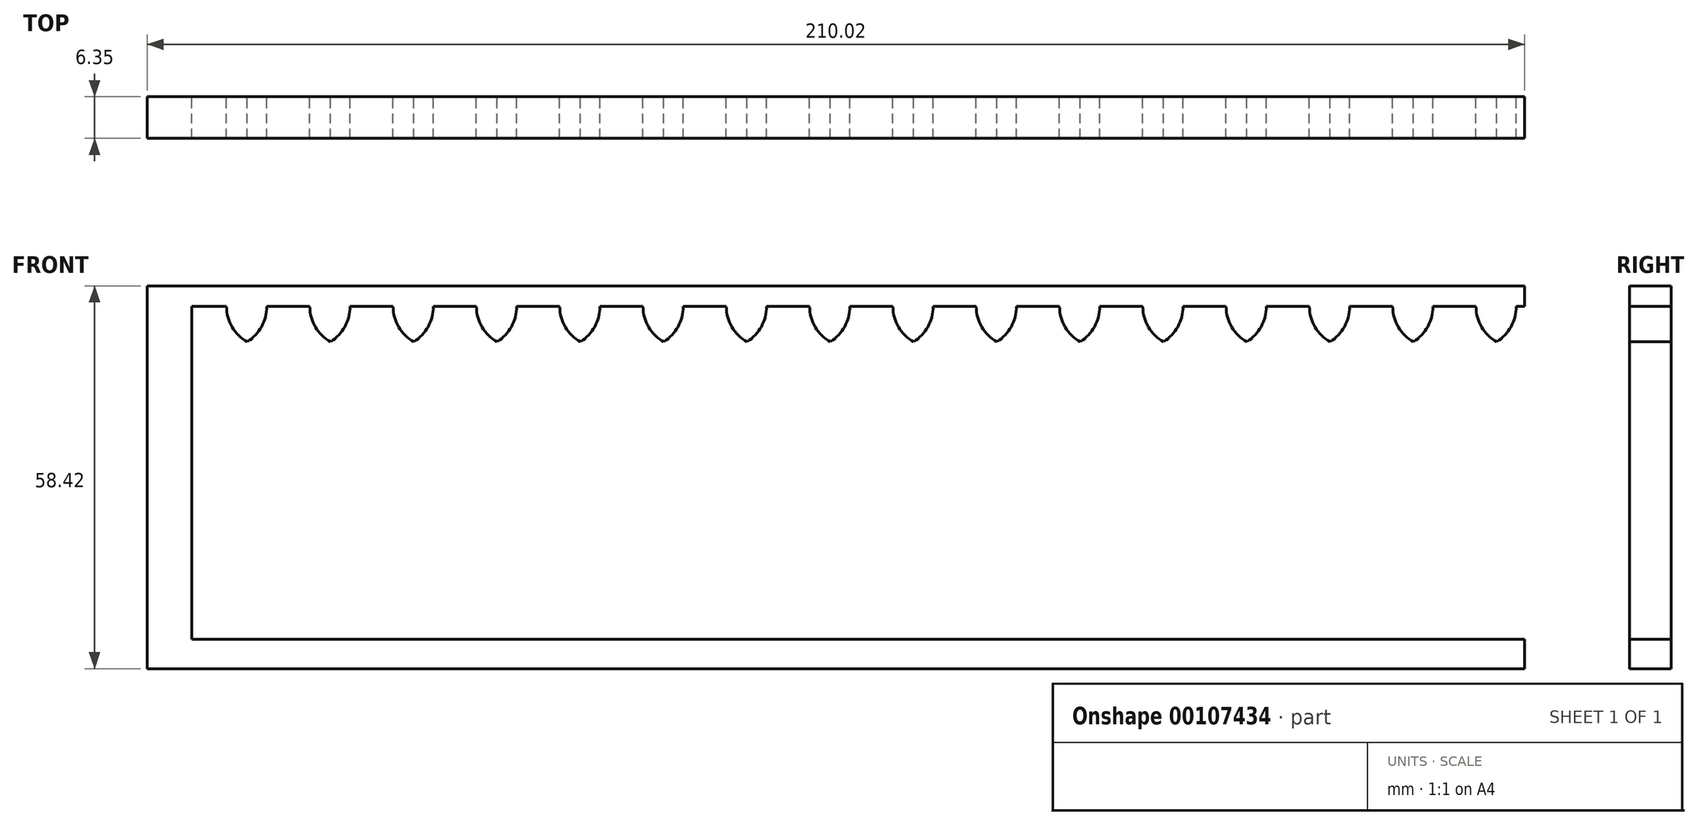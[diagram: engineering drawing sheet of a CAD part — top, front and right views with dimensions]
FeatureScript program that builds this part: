
annotation { "Feature Type Name" : "Feature", "Feature Type Description" : "" }
export const myFeature = defineFeature(function(context is Context, id is Id, definition is map)
    precondition{}
    {
        {
            var Q0;
            Q0=qCreatedBy(makeId("Front.planeOp"),FACE);
            var sketch = newSketch(context, id + "F0", { "sketchPlane" : qUnion([Q0])});
            skLineSegment(sketch, "E0.bottom", {"start": v(-100.17, 36.3) * mm, "end": v(103.03, 36.3) * mm});
            skLineSegment(sketch, "E0.top", {"start": v(-100.17, -14.5) * mm, "end": v(103.03, -14.5) * mm});
            skLineSegment(sketch, "E0.left", {"start": v(-100.17, 36.3) * mm, "end": v(-100.17, -14.5) * mm});
            skArc(sketch, "E1", {"start": v(-91.7, 30.93) * mm, "mid": v(-89.52, 33.23) * mm, "end": v(-88.73, 36.3) * mm});
            skArc(sketch, "E2", {"start": v(-94.87, 36.3) * mm, "mid": v(-94.02, 33.18) * mm, "end": v(-91.7, 30.93) * mm});
            skArc(sketch, "E3.1.0.0", {"start": v(-79, 30.93) * mm, "mid": v(-76.82, 33.23) * mm, "end": v(-76.03, 36.3) * mm});
            skArc(sketch, "E3.1.0.1", {"start": v(-82.17, 36.3) * mm, "mid": v(-81.32, 33.18) * mm, "end": v(-79, 30.93) * mm});
            skArc(sketch, "E3.2.0.0", {"start": v(-66.3, 30.93) * mm, "mid": v(-64.12, 33.23) * mm, "end": v(-63.33, 36.3) * mm});
            skArc(sketch, "E3.2.0.1", {"start": v(-69.47, 36.3) * mm, "mid": v(-68.62, 33.18) * mm, "end": v(-66.3, 30.93) * mm});
            skArc(sketch, "E3.3.0.0", {"start": v(-53.6, 30.93) * mm, "mid": v(-51.42, 33.23) * mm, "end": v(-50.63, 36.3) * mm});
            skArc(sketch, "E3.3.0.1", {"start": v(-56.77, 36.3) * mm, "mid": v(-55.92, 33.18) * mm, "end": v(-53.6, 30.93) * mm});
            skArc(sketch, "E3.4.0.0", {"start": v(-40.9, 30.93) * mm, "mid": v(-38.72, 33.23) * mm, "end": v(-37.93, 36.3) * mm});
            skArc(sketch, "E3.4.0.1", {"start": v(-44.07, 36.3) * mm, "mid": v(-43.22, 33.18) * mm, "end": v(-40.9, 30.93) * mm});
            skArc(sketch, "E3.5.0.0", {"start": v(-28.2, 30.93) * mm, "mid": v(-26.02, 33.23) * mm, "end": v(-25.23, 36.3) * mm});
            skArc(sketch, "E3.5.0.1", {"start": v(-31.37, 36.3) * mm, "mid": v(-30.52, 33.18) * mm, "end": v(-28.2, 30.93) * mm});
            skArc(sketch, "E3.6.0.0", {"start": v(-15.5, 30.93) * mm, "mid": v(-13.32, 33.23) * mm, "end": v(-12.53, 36.3) * mm});
            skArc(sketch, "E3.6.0.1", {"start": v(-18.67, 36.3) * mm, "mid": v(-17.82, 33.18) * mm, "end": v(-15.5, 30.93) * mm});
            skArc(sketch, "E3.7.0.0", {"start": v(-2.8, 30.93) * mm, "mid": v(-0.62, 33.23) * mm, "end": v(0.17, 36.3) * mm});
            skArc(sketch, "E3.7.0.1", {"start": v(-5.97, 36.3) * mm, "mid": v(-5.12, 33.18) * mm, "end": v(-2.8, 30.93) * mm});
            skArc(sketch, "E3.8.0.0", {"start": v(9.9, 30.93) * mm, "mid": v(12.08, 33.23) * mm, "end": v(12.87, 36.3) * mm});
            skArc(sketch, "E3.8.0.1", {"start": v(6.73, 36.3) * mm, "mid": v(7.58, 33.18) * mm, "end": v(9.9, 30.93) * mm});
            skArc(sketch, "E3.9.0.0", {"start": v(22.6, 30.93) * mm, "mid": v(24.78, 33.23) * mm, "end": v(25.57, 36.3) * mm});
            skArc(sketch, "E3.9.0.1", {"start": v(19.43, 36.3) * mm, "mid": v(20.28, 33.18) * mm, "end": v(22.6, 30.93) * mm});
            skArc(sketch, "E3.10.0.0", {"start": v(35.3, 30.93) * mm, "mid": v(37.48, 33.23) * mm, "end": v(38.27, 36.3) * mm});
            skArc(sketch, "E3.10.0.1", {"start": v(32.13, 36.3) * mm, "mid": v(32.98, 33.18) * mm, "end": v(35.3, 30.93) * mm});
            skArc(sketch, "E3.11.0.0", {"start": v(48, 30.93) * mm, "mid": v(50.18, 33.23) * mm, "end": v(50.97, 36.3) * mm});
            skArc(sketch, "E3.11.0.1", {"start": v(44.83, 36.3) * mm, "mid": v(45.68, 33.18) * mm, "end": v(48, 30.93) * mm});
            skArc(sketch, "E3.12.0.0", {"start": v(60.7, 30.93) * mm, "mid": v(62.88, 33.23) * mm, "end": v(63.67, 36.3) * mm});
            skArc(sketch, "E3.12.0.1", {"start": v(57.53, 36.3) * mm, "mid": v(58.38, 33.18) * mm, "end": v(60.7, 30.93) * mm});
            skArc(sketch, "E3.13.0.0", {"start": v(73.4, 30.93) * mm, "mid": v(75.58, 33.23) * mm, "end": v(76.37, 36.3) * mm});
            skArc(sketch, "E3.13.0.1", {"start": v(70.23, 36.3) * mm, "mid": v(71.08, 33.18) * mm, "end": v(73.4, 30.93) * mm});
            skArc(sketch, "E3.14.0.0", {"start": v(86.1, 30.93) * mm, "mid": v(88.28, 33.23) * mm, "end": v(89.07, 36.3) * mm});
            skArc(sketch, "E3.14.0.1", {"start": v(82.93, 36.3) * mm, "mid": v(83.78, 33.18) * mm, "end": v(86.1, 30.93) * mm});
            skArc(sketch, "E3.15.0.0", {"start": v(98.8, 30.93) * mm, "mid": v(100.98, 33.23) * mm, "end": v(101.77, 36.3) * mm});
            skArc(sketch, "E3.15.0.1", {"start": v(95.63, 36.3) * mm, "mid": v(96.48, 33.18) * mm, "end": v(98.8, 30.93) * mm});
            skLineSegment(sketch, "E3.direction1", {"start": v(-91.7, 30.93) * mm, "end": v(-79, 30.93) * mm, "construction": true});
            skArc(sketch, "E4.MirrorCS", {"start": v(-94.87, -14.5) * mm, "mid": v(-94.02, -11.38) * mm, "end": v(-91.7, -9.13) * mm});
            skArc(sketch, "E5.MirrorCS", {"start": v(-91.7, -9.13) * mm, "mid": v(-89.52, -11.43) * mm, "end": v(-88.73, -14.5) * mm});
            skArc(sketch, "E6.MirrorCS", {"start": v(-82.17, -14.5) * mm, "mid": v(-81.32, -11.38) * mm, "end": v(-79, -9.13) * mm});
            skArc(sketch, "E7.MirrorCS", {"start": v(-79, -9.13) * mm, "mid": v(-76.82, -11.43) * mm, "end": v(-76.03, -14.5) * mm});
            skArc(sketch, "E8.MirrorCS", {"start": v(-69.47, -14.5) * mm, "mid": v(-68.62, -11.38) * mm, "end": v(-66.3, -9.13) * mm});
            skArc(sketch, "E9.MirrorCS", {"start": v(-66.3, -9.13) * mm, "mid": v(-64.12, -11.43) * mm, "end": v(-63.33, -14.5) * mm});
            skArc(sketch, "E10.MirrorCS", {"start": v(-56.77, -14.5) * mm, "mid": v(-55.92, -11.38) * mm, "end": v(-53.6, -9.13) * mm});
            skArc(sketch, "E11.MirrorCS", {"start": v(-53.6, -9.13) * mm, "mid": v(-51.42, -11.43) * mm, "end": v(-50.63, -14.5) * mm});
            skArc(sketch, "E12.MirrorCS", {"start": v(-44.07, -14.5) * mm, "mid": v(-43.22, -11.38) * mm, "end": v(-40.9, -9.13) * mm});
            skArc(sketch, "E13.MirrorCS", {"start": v(-40.9, -9.13) * mm, "mid": v(-38.72, -11.43) * mm, "end": v(-37.93, -14.5) * mm});
            skArc(sketch, "E14.MirrorCS", {"start": v(-31.37, -14.5) * mm, "mid": v(-30.52, -11.38) * mm, "end": v(-28.2, -9.13) * mm});
            skArc(sketch, "E15.MirrorCS", {"start": v(-28.2, -9.13) * mm, "mid": v(-26.02, -11.43) * mm, "end": v(-25.23, -14.5) * mm});
            skArc(sketch, "E16.MirrorCS", {"start": v(-18.67, -14.5) * mm, "mid": v(-17.82, -11.38) * mm, "end": v(-15.5, -9.13) * mm});
            skArc(sketch, "E17.MirrorCS", {"start": v(-15.5, -9.13) * mm, "mid": v(-13.32, -11.43) * mm, "end": v(-12.53, -14.5) * mm});
            skArc(sketch, "E18.MirrorCS", {"start": v(-5.97, -14.5) * mm, "mid": v(-5.12, -11.38) * mm, "end": v(-2.8, -9.13) * mm});
            skArc(sketch, "E19.MirrorCS", {"start": v(-2.8, -9.13) * mm, "mid": v(-0.62, -11.43) * mm, "end": v(0.17, -14.5) * mm});
            skArc(sketch, "E20.MirrorCS", {"start": v(6.73, -14.5) * mm, "mid": v(7.58, -11.38) * mm, "end": v(9.9, -9.13) * mm});
            skArc(sketch, "E21.MirrorCS", {"start": v(9.9, -9.13) * mm, "mid": v(12.08, -11.43) * mm, "end": v(12.87, -14.5) * mm});
            skArc(sketch, "E22.MirrorCS", {"start": v(19.43, -14.5) * mm, "mid": v(20.28, -11.38) * mm, "end": v(22.6, -9.13) * mm});
            skArc(sketch, "E23.MirrorCS", {"start": v(22.6, -9.13) * mm, "mid": v(24.78, -11.43) * mm, "end": v(25.57, -14.5) * mm});
            skArc(sketch, "E24.MirrorCS", {"start": v(32.13, -14.5) * mm, "mid": v(32.98, -11.38) * mm, "end": v(35.3, -9.13) * mm});
            skArc(sketch, "E25.MirrorCS", {"start": v(35.3, -9.13) * mm, "mid": v(37.48, -11.43) * mm, "end": v(38.27, -14.5) * mm});
            skArc(sketch, "E26.MirrorCS", {"start": v(44.83, -14.5) * mm, "mid": v(45.68, -11.38) * mm, "end": v(48, -9.13) * mm});
            skArc(sketch, "E27.MirrorCS", {"start": v(48, -9.13) * mm, "mid": v(50.18, -11.43) * mm, "end": v(50.97, -14.5) * mm});
            skArc(sketch, "E28.MirrorCS", {"start": v(57.53, -14.5) * mm, "mid": v(58.38, -11.38) * mm, "end": v(60.7, -9.13) * mm});
            skArc(sketch, "E29.MirrorCS", {"start": v(60.7, -9.13) * mm, "mid": v(62.88, -11.43) * mm, "end": v(63.67, -14.5) * mm});
            skArc(sketch, "E30.MirrorCS", {"start": v(70.23, -14.5) * mm, "mid": v(71.08, -11.38) * mm, "end": v(73.4, -9.13) * mm});
            skArc(sketch, "E31.MirrorCS", {"start": v(73.4, -9.13) * mm, "mid": v(75.58, -11.43) * mm, "end": v(76.37, -14.5) * mm});
            skArc(sketch, "E32.MirrorCS", {"start": v(82.93, -14.5) * mm, "mid": v(83.78, -11.38) * mm, "end": v(86.1, -9.13) * mm});
            skArc(sketch, "E33.MirrorCS", {"start": v(86.1, -9.13) * mm, "mid": v(88.28, -11.43) * mm, "end": v(89.07, -14.5) * mm});
            skArc(sketch, "E34.MirrorCS", {"start": v(95.63, -14.5) * mm, "mid": v(96.48, -11.38) * mm, "end": v(98.8, -9.13) * mm});
            skArc(sketch, "E35.MirrorCS", {"start": v(98.8, -9.13) * mm, "mid": v(100.98, -11.43) * mm, "end": v(101.77, -14.5) * mm});
            skLineSegment(sketch, "E36.bottom", {"start": v(-107, 39.46) * mm, "end": v(103.03, 39.46) * mm});
            skLineSegment(sketch, "E36.top", {"start": v(-107, -18.96) * mm, "end": v(103.03, -18.96) * mm});
            skLineSegment(sketch, "E36.left", {"start": v(-107, 39.46) * mm, "end": v(-107, -18.96) * mm});
            skLineSegment(sketch, "E37", {"start": v(103.03, 36.3) * mm, "end": v(103.03, 39.46) * mm});
            skLineSegment(sketch, "E38", {"start": v(103.03, -14.5) * mm, "end": v(103.03, -18.96) * mm});
            skSolve(sketch);
        }
        {
            var Q0;
            {var subQ30=sQuery(id+"F0.wireOp",EDGE,"E0.left");Q0=makeQuery(id+"F0.imprint","IMPRINT",FACE,{"disambiguationData":[TD([[makeQuery(id+"F0.imprint","IMPRINT",EDGE,{"derivedFrom":subQ30}),-1.0]])]});}
            var Q1;
            {var subQ0=sQuery(id+"F0.wireOp",EDGE,"E1");Q1=makeQuery(id+"F0.imprint","IMPRINT",FACE,{"disambiguationData":[TD([[makeQuery(id+"F0.imprint","IMPRINT",EDGE,{"derivedFrom":subQ0}),1.0]])]});}
            var Q2;
            {var subQ0=sQuery(id+"F0.wireOp",EDGE,"E3.1.0.0");Q2=makeQuery(id+"F0.imprint","IMPRINT",FACE,{"disambiguationData":[TD([[makeQuery(id+"F0.imprint","IMPRINT",EDGE,{"derivedFrom":subQ0}),1.0]])]});}
            var Q3;
            {var subQ0=sQuery(id+"F0.wireOp",EDGE,"E3.2.0.0");Q3=makeQuery(id+"F0.imprint","IMPRINT",FACE,{"disambiguationData":[TD([[makeQuery(id+"F0.imprint","IMPRINT",EDGE,{"derivedFrom":subQ0}),1.0]])]});}
            var Q4;
            {var subQ0=sQuery(id+"F0.wireOp",EDGE,"E3.3.0.0");Q4=makeQuery(id+"F0.imprint","IMPRINT",FACE,{"disambiguationData":[TD([[makeQuery(id+"F0.imprint","IMPRINT",EDGE,{"derivedFrom":subQ0}),1.0]])]});}
            var Q5;
            {var subQ0=sQuery(id+"F0.wireOp",EDGE,"E3.4.0.0");Q5=makeQuery(id+"F0.imprint","IMPRINT",FACE,{"disambiguationData":[TD([[makeQuery(id+"F0.imprint","IMPRINT",EDGE,{"derivedFrom":subQ0}),1.0]])]});}
            var Q6;
            {var subQ0=sQuery(id+"F0.wireOp",EDGE,"E3.5.0.0");Q6=makeQuery(id+"F0.imprint","IMPRINT",FACE,{"disambiguationData":[TD([[makeQuery(id+"F0.imprint","IMPRINT",EDGE,{"derivedFrom":subQ0}),1.0]])]});}
            var Q7;
            {var subQ0=sQuery(id+"F0.wireOp",EDGE,"E3.6.0.0");Q7=makeQuery(id+"F0.imprint","IMPRINT",FACE,{"disambiguationData":[TD([[makeQuery(id+"F0.imprint","IMPRINT",EDGE,{"derivedFrom":subQ0}),1.0]])]});}
            var Q8;
            {var subQ0=sQuery(id+"F0.wireOp",EDGE,"E3.7.0.0");Q8=makeQuery(id+"F0.imprint","IMPRINT",FACE,{"disambiguationData":[TD([[makeQuery(id+"F0.imprint","IMPRINT",EDGE,{"derivedFrom":subQ0}),1.0]])]});}
            var Q9;
            {var subQ0=sQuery(id+"F0.wireOp",EDGE,"E3.8.0.0");Q9=makeQuery(id+"F0.imprint","IMPRINT",FACE,{"disambiguationData":[TD([[makeQuery(id+"F0.imprint","IMPRINT",EDGE,{"derivedFrom":subQ0}),1.0]])]});}
            var Q10;
            {var subQ0=sQuery(id+"F0.wireOp",EDGE,"E3.9.0.0");Q10=makeQuery(id+"F0.imprint","IMPRINT",FACE,{"disambiguationData":[TD([[makeQuery(id+"F0.imprint","IMPRINT",EDGE,{"derivedFrom":subQ0}),1.0]])]});}
            var Q11;
            {var subQ0=sQuery(id+"F0.wireOp",EDGE,"E3.10.0.0");Q11=makeQuery(id+"F0.imprint","IMPRINT",FACE,{"disambiguationData":[TD([[makeQuery(id+"F0.imprint","IMPRINT",EDGE,{"derivedFrom":subQ0}),1.0]])]});}
            var Q12;
            {var subQ0=sQuery(id+"F0.wireOp",EDGE,"E3.11.0.0");Q12=makeQuery(id+"F0.imprint","IMPRINT",FACE,{"disambiguationData":[TD([[makeQuery(id+"F0.imprint","IMPRINT",EDGE,{"derivedFrom":subQ0}),1.0]])]});}
            var Q13;
            {var subQ0=sQuery(id+"F0.wireOp",EDGE,"E3.12.0.0");Q13=makeQuery(id+"F0.imprint","IMPRINT",FACE,{"disambiguationData":[TD([[makeQuery(id+"F0.imprint","IMPRINT",EDGE,{"derivedFrom":subQ0}),1.0]])]});}
            var Q14;
            {var subQ0=sQuery(id+"F0.wireOp",EDGE,"E3.13.0.0");Q14=makeQuery(id+"F0.imprint","IMPRINT",FACE,{"disambiguationData":[TD([[makeQuery(id+"F0.imprint","IMPRINT",EDGE,{"derivedFrom":subQ0}),1.0]])]});}
            var Q15;
            {var subQ0=sQuery(id+"F0.wireOp",EDGE,"E3.14.0.0");Q15=makeQuery(id+"F0.imprint","IMPRINT",FACE,{"disambiguationData":[TD([[makeQuery(id+"F0.imprint","IMPRINT",EDGE,{"derivedFrom":subQ0}),1.0]])]});}
            var Q16;
            {var subQ0=sQuery(id+"F0.wireOp",EDGE,"E3.15.0.0");Q16=makeQuery(id+"F0.imprint","IMPRINT",FACE,{"disambiguationData":[TD([[makeQuery(id+"F0.imprint","IMPRINT",EDGE,{"derivedFrom":subQ0}),1.0]])]});}
            var Q17;
            {var subQ0=sQuery(id+"F0.wireOp",EDGE,"E34.MirrorCS");Q17=makeQuery(id+"F0.imprint","IMPRINT",FACE,{"disambiguationData":[TD([[makeQuery(id+"F0.imprint","IMPRINT",EDGE,{"derivedFrom":subQ0}),-1.0]])]});}
            var Q18;
            {var subQ0=sQuery(id+"F0.wireOp",EDGE,"E32.MirrorCS");Q18=makeQuery(id+"F0.imprint","IMPRINT",FACE,{"disambiguationData":[TD([[makeQuery(id+"F0.imprint","IMPRINT",EDGE,{"derivedFrom":subQ0}),-1.0]])]});}
            var Q19;
            {var subQ0=sQuery(id+"F0.wireOp",EDGE,"E30.MirrorCS");Q19=makeQuery(id+"F0.imprint","IMPRINT",FACE,{"disambiguationData":[TD([[makeQuery(id+"F0.imprint","IMPRINT",EDGE,{"derivedFrom":subQ0}),-1.0]])]});}
            var Q20;
            {var subQ0=sQuery(id+"F0.wireOp",EDGE,"E28.MirrorCS");Q20=makeQuery(id+"F0.imprint","IMPRINT",FACE,{"disambiguationData":[TD([[makeQuery(id+"F0.imprint","IMPRINT",EDGE,{"derivedFrom":subQ0}),-1.0]])]});}
            var Q21;
            {var subQ0=sQuery(id+"F0.wireOp",EDGE,"E26.MirrorCS");Q21=makeQuery(id+"F0.imprint","IMPRINT",FACE,{"disambiguationData":[TD([[makeQuery(id+"F0.imprint","IMPRINT",EDGE,{"derivedFrom":subQ0}),-1.0]])]});}
            var Q22;
            {var subQ0=sQuery(id+"F0.wireOp",EDGE,"E24.MirrorCS");Q22=makeQuery(id+"F0.imprint","IMPRINT",FACE,{"disambiguationData":[TD([[makeQuery(id+"F0.imprint","IMPRINT",EDGE,{"derivedFrom":subQ0}),-1.0]])]});}
            var Q23;
            {var subQ0=sQuery(id+"F0.wireOp",EDGE,"E22.MirrorCS");Q23=makeQuery(id+"F0.imprint","IMPRINT",FACE,{"disambiguationData":[TD([[makeQuery(id+"F0.imprint","IMPRINT",EDGE,{"derivedFrom":subQ0}),-1.0]])]});}
            var Q24;
            {var subQ0=sQuery(id+"F0.wireOp",EDGE,"E20.MirrorCS");Q24=makeQuery(id+"F0.imprint","IMPRINT",FACE,{"disambiguationData":[TD([[makeQuery(id+"F0.imprint","IMPRINT",EDGE,{"derivedFrom":subQ0}),-1.0]])]});}
            var Q25;
            {var subQ0=sQuery(id+"F0.wireOp",EDGE,"E18.MirrorCS");Q25=makeQuery(id+"F0.imprint","IMPRINT",FACE,{"disambiguationData":[TD([[makeQuery(id+"F0.imprint","IMPRINT",EDGE,{"derivedFrom":subQ0}),-1.0]])]});}
            var Q26;
            {var subQ0=sQuery(id+"F0.wireOp",EDGE,"E16.MirrorCS");Q26=makeQuery(id+"F0.imprint","IMPRINT",FACE,{"disambiguationData":[TD([[makeQuery(id+"F0.imprint","IMPRINT",EDGE,{"derivedFrom":subQ0}),-1.0]])]});}
            var Q27;
            {var subQ0=sQuery(id+"F0.wireOp",EDGE,"E14.MirrorCS");Q27=makeQuery(id+"F0.imprint","IMPRINT",FACE,{"disambiguationData":[TD([[makeQuery(id+"F0.imprint","IMPRINT",EDGE,{"derivedFrom":subQ0}),-1.0]])]});}
            var Q28;
            {var subQ0=sQuery(id+"F0.wireOp",EDGE,"E12.MirrorCS");Q28=makeQuery(id+"F0.imprint","IMPRINT",FACE,{"disambiguationData":[TD([[makeQuery(id+"F0.imprint","IMPRINT",EDGE,{"derivedFrom":subQ0}),-1.0]])]});}
            var Q29;
            {var subQ0=sQuery(id+"F0.wireOp",EDGE,"E10.MirrorCS");Q29=makeQuery(id+"F0.imprint","IMPRINT",FACE,{"disambiguationData":[TD([[makeQuery(id+"F0.imprint","IMPRINT",EDGE,{"derivedFrom":subQ0}),-1.0]])]});}
            var Q30;
            {var subQ0=sQuery(id+"F0.wireOp",EDGE,"E8.MirrorCS");Q30=makeQuery(id+"F0.imprint","IMPRINT",FACE,{"disambiguationData":[TD([[makeQuery(id+"F0.imprint","IMPRINT",EDGE,{"derivedFrom":subQ0}),-1.0]])]});}
            var Q31;
            {var subQ0=sQuery(id+"F0.wireOp",EDGE,"E6.MirrorCS");Q31=makeQuery(id+"F0.imprint","IMPRINT",FACE,{"disambiguationData":[TD([[makeQuery(id+"F0.imprint","IMPRINT",EDGE,{"derivedFrom":subQ0}),-1.0]])]});}
            var Q32;
            {var subQ0=sQuery(id+"F0.wireOp",EDGE,"E4.MirrorCS");Q32=makeQuery(id+"F0.imprint","IMPRINT",FACE,{"disambiguationData":[TD([[makeQuery(id+"F0.imprint","IMPRINT",EDGE,{"derivedFrom":subQ0}),-1.0]])]});}
            extrude(context, id + "F1", {"entities" : qUnion([Q0, Q1, Q2, Q3, Q4, Q5, Q6, Q7, Q8, Q9, Q10, Q11, Q12, Q13, Q14, Q15, Q16, Q17, Q18, Q19, Q20, Q21, Q22, Q23, Q24, Q25, Q26, Q27, Q28, Q29, Q30, Q31, Q32]), "depth" : 6.35 * mm});
        }
    });
